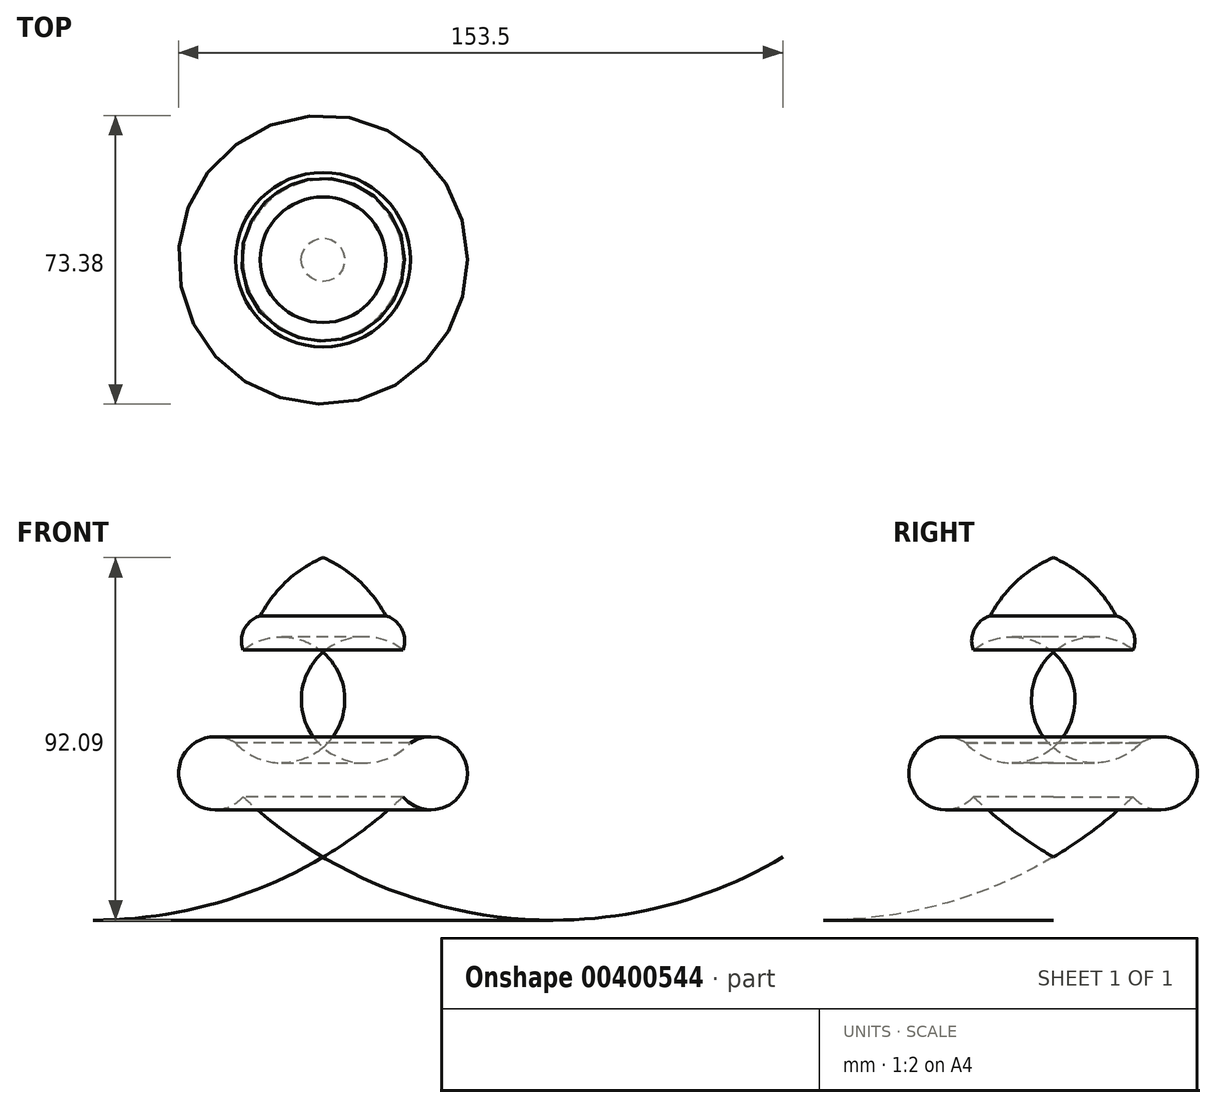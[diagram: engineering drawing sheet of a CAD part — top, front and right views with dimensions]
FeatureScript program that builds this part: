
annotation { "Feature Type Name" : "Feature", "Feature Type Description" : "" }
export const myFeature = defineFeature(function(context is Context, id is Id, definition is map)
    precondition{}
    {
        {
            var Q0;
            Q0=qCreatedBy(makeId("Front.planeOp"),FACE);
            var sketch = newSketch(context, id + "F0", { "sketchPlane" : qUnion([Q0])});
            skLineSegment(sketch, "E0", {"start": v(0, 76.07) * mm, "end": v(0, -3.15) * mm});
            skLineSegment(sketch, "E1", {"start": v(0, -3.15) * mm, "end": v(0, -77.05) * mm});
            skArc(sketch, "E2", {"start": v(15.96, 61.29) * mm, "mid": v(9.27, 70.07) * mm, "end": v(0, 76.07) * mm});
            skArc(sketch, "E3", {"start": v(20.3, 52.62) * mm, "mid": v(20.02, 57.9) * mm, "end": v(15.96, 61.29) * mm});
            skArc(sketch, "E4", {"start": v(22.18, 28.95) * mm, "mid": v(26.48, 41.2) * mm, "end": v(20.3, 52.62) * mm});
            skArc(sketch, "E5", {"start": v(20.3, 15.33) * mm, "mid": v(36.6, 20.02) * mm, "end": v(22.18, 28.95) * mm});
            skArc(sketch, "E6", {"start": v(0, 0) * mm, "mid": v(10.58, 7.1) * mm, "end": v(20.3, 15.33) * mm});
            skPoint(sketch, "E7.orphan", {"position": v(20.3, 27.25) * mm});
            skSolve(sketch);
        }
        {
            var Q0;
            {var subQ5=sQuery(id+"F0.wireOp",EDGE,"E2");Q0=makeQuery(id+"F0.imprint","IMPRINT",FACE,{"disambiguationData":[TD([[makeQuery(id+"F0.imprint","IMPRINT",EDGE,{"derivedFrom":subQ5}),1.0]])]});}
            var Q1;
            Q1=sQuery(id+"F0.wireOp",EDGE,"E0");
            revolve(context, id + "F1", {"entities" : qUnion([Q0]), "axis" : qUnion([Q1]), "revolveType" : RevolveType.FULL});
        }
    });
